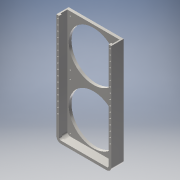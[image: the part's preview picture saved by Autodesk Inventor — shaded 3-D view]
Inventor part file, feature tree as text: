
AUTODESK INVENTOR PART (.ipt)
format: ipt  version: 2016 (Build 200138000, 138)  size: 243,200 bytes
history: native  units: mm
features: sketch x6, projected_geometry x6, extrude x4, hole x2
ambient origin geometry x8: Origin, YZ Plane, XZ Plane, XY Plane, X Axis, Y Axis, Z Axis, Center Point
bodies: Solid1 (feature_tree)
feature tree (18):
  extrude  "Extrusion1"  Depth=240.0mm
  extrude  "Extrusion2"  Depth=6.0mm
  extrude  "Extrusion3"  Depth=6.0mm
  extrude  "Extrusion4"  Depth=3.0mm
  hole  "Hole1"  [1 undecoded]
  hole  "Hole2"  [1 undecoded]
  sketch  "Sketch1"  dims[d0=120.0mm d1=240.0mm]
  sketch  "Sketch2"  dims[d2=120.0mm d3=6.0mm]
  projected_geometry  "Projected Loop1"
  sketch  "Sketch3"  dims[d4=10.0mm d5=6.0mm]
  projected_geometry  "Projected Loop2"
  sketch  "Sketch5"  dims[d6=0.0mm d7=3.0mm]
  projected_geometry  "Projected Loop3"
  sketch  "Sketch6"  dims[d8=15.0mm d9=0.0mm]
  projected_geometry  "Projected Loop4"
  sketch  "Sketch7"  dims[d10=3.0mm d11=6.0mm d12=0.0mm d13=6.0mm d14=0.0mm d15=18.0mm d16=9.0mm d17=3.1mm d18=6.0mm d19=4.0mm d20=2.0mm d21=90.0deg d22=4.0mm d23=20.594885mm d24=6.0mm d25=160.0mm d27=12.0mm d28=10.0mm d30=10.0mm d32=3.1mm d33=6.0mm d34=4.0mm d35=2.0mm d36=90.0deg d37=4.0mm d38=20.594885mm]
  projected_geometry  "Projected Loop5"
  projected_geometry  "Projected Loop6"
note: 2 required parameter values undecoded (feature->parameter linkage not recoverable at this tier; creation-order binding heuristic only, values carry confidence <= 0.55)
